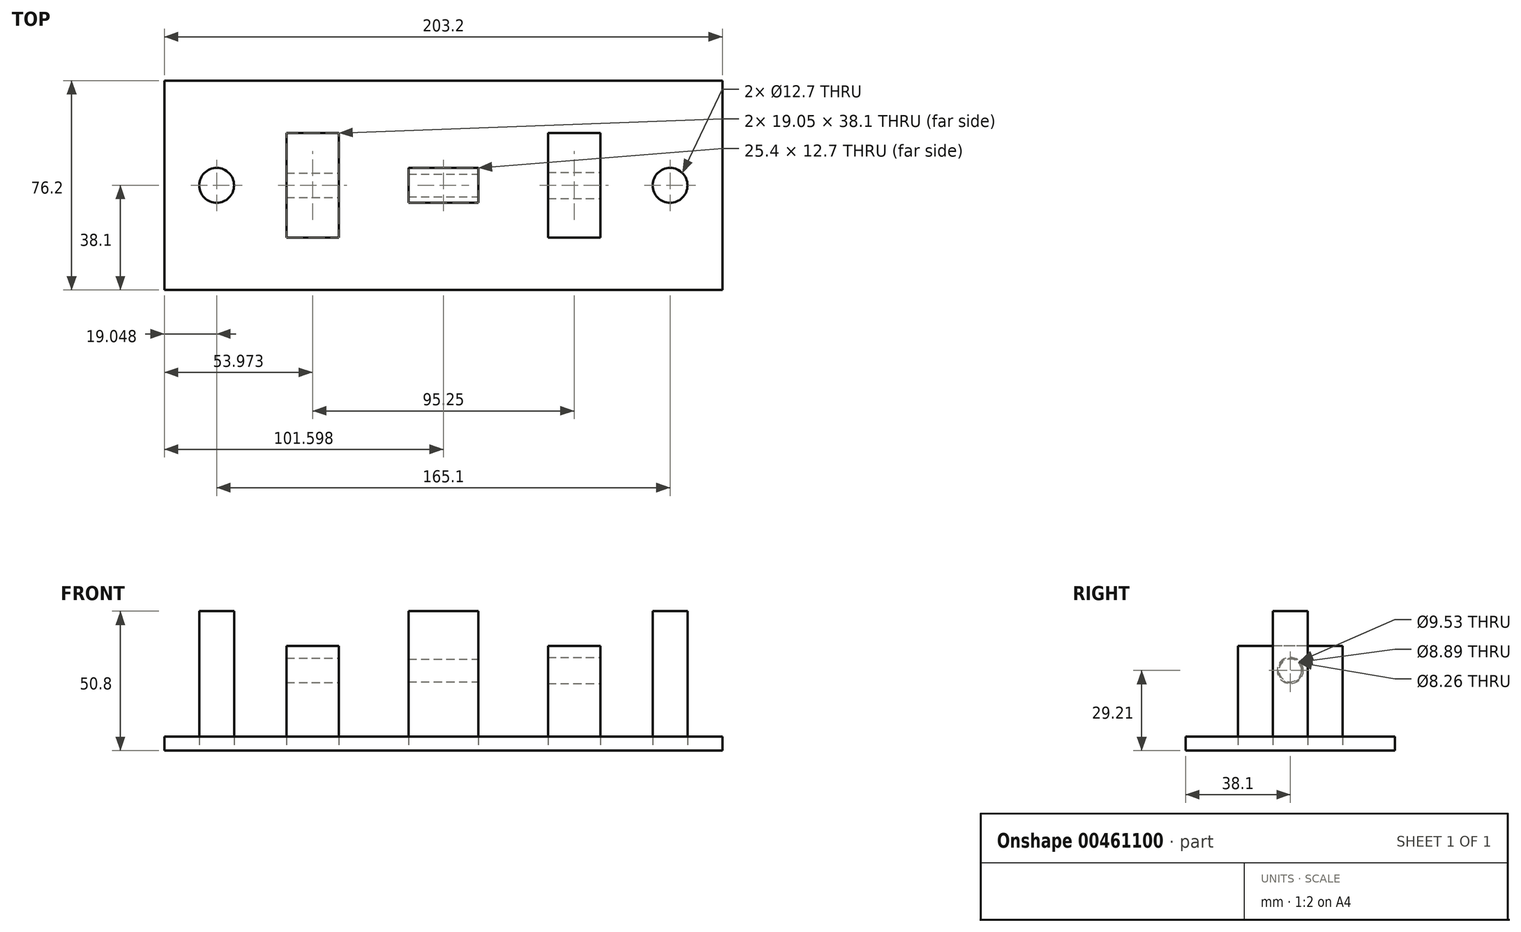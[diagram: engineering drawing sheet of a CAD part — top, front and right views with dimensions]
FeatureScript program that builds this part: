
annotation { "Feature Type Name" : "Feature", "Feature Type Description" : "" }
export const myFeature = defineFeature(function(context is Context, id is Id, definition is map)
    precondition{}
    {
        {
            var Q0;
            Q0=qCreatedBy(makeId("Top.planeOp"),FACE);
            var sketch = newSketch(context, id + "F0", { "sketchPlane" : qUnion([Q0])});
            skLineSegment(sketch, "E0.bottom", {"start": v(-155.23, 38.1) * mm, "end": v(47.97, 38.1) * mm});
            skLineSegment(sketch, "E0.top", {"start": v(-155.23, -38.1) * mm, "end": v(47.97, -38.1) * mm});
            skLineSegment(sketch, "E0.left", {"start": v(-155.23, 38.1) * mm, "end": v(-155.23, -38.1) * mm});
            skLineSegment(sketch, "E0.right", {"start": v(47.97, 38.1) * mm, "end": v(47.97, -38.1) * mm});
            skCircle(sketch, "E1", {"center": v(-136.18, 0) * mm, "radius": 6.35 * mm});
            skCircle(sketch, "E2", {"center": v(28.92, 0) * mm, "radius": 6.35 * mm});
            skLineSegment(sketch, "E3.bottom", {"start": v(-66.33, 6.35) * mm, "end": v(-40.93, 6.35) * mm});
            skLineSegment(sketch, "E3.top", {"start": v(-66.33, -6.35) * mm, "end": v(-40.93, -6.35) * mm});
            skLineSegment(sketch, "E3.left", {"start": v(-66.33, 6.35) * mm, "end": v(-66.33, -6.35) * mm});
            skLineSegment(sketch, "E3.right", {"start": v(-40.93, 6.35) * mm, "end": v(-40.93, -6.35) * mm});
            skPoint(sketch, "E3.middle", {"position": v(-53.63, 0) * mm});
            skLineSegment(sketch, "E4", {"start": v(28.92, 0) * mm, "end": v(47.97, 0) * mm});
            skLineSegment(sketch, "E5.bottom", {"start": v(-110.78, 19.05) * mm, "end": v(-91.73, 19.05) * mm});
            skLineSegment(sketch, "E5.top", {"start": v(-110.78, -19.05) * mm, "end": v(-91.73, -19.05) * mm});
            skLineSegment(sketch, "E5.left", {"start": v(-110.78, 19.05) * mm, "end": v(-110.78, -19.05) * mm});
            skLineSegment(sketch, "E5.right", {"start": v(-91.73, 19.05) * mm, "end": v(-91.73, -19.05) * mm});
            skPoint(sketch, "E5.middle", {"position": v(-101.26, 0) * mm});
            skLineSegment(sketch, "E6.bottom", {"start": v(-15.53, 19.05) * mm, "end": v(3.52, 19.05) * mm});
            skLineSegment(sketch, "E6.top", {"start": v(-15.53, -19.05) * mm, "end": v(3.52, -19.05) * mm});
            skLineSegment(sketch, "E6.left", {"start": v(-15.53, 19.05) * mm, "end": v(-15.53, -19.05) * mm});
            skLineSegment(sketch, "E6.right", {"start": v(3.52, 19.05) * mm, "end": v(3.52, -19.05) * mm});
            skPoint(sketch, "E6.middle", {"position": v(-6, 0) * mm});
            skSolve(sketch);
        }
        {
            var Q0;
            Q0=makeQuery(id+"F0.imprint","IMPRINT",FACE,{"disambiguationData":[TD([[makeQuery(id+"F0.imprint","IMPRINT",EDGE,{"derivedFrom":sQuery(id+"F0.wireOp",EDGE,"E3.bottom")}),-1.0]])]});
            var Q1;
            Q1=makeQuery(id+"F0.imprint","IMPRINT",FACE,{"disambiguationData":[TD([[makeQuery(id+"F0.imprint","IMPRINT",EDGE,{"derivedFrom":sQuery(id+"F0.wireOp",EDGE,"E2")}),1.0]])]});
            var Q2;
            Q2=makeQuery(id+"F0.imprint","IMPRINT",FACE,{"disambiguationData":[TD([[makeQuery(id+"F0.imprint","IMPRINT",EDGE,{"derivedFrom":sQuery(id+"F0.wireOp",EDGE,"E1")}),1.0]])]});
            extrude(context, id + "F1", {"entities" : qUnion([Q0, Q1, Q2]), "depth" : 50.8 * mm});
        }
        {
            var Q0;
            Q0=makeQuery(id+"F0.imprint","IMPRINT",FACE,{"disambiguationData":[TD([[makeQuery(id+"F0.imprint","IMPRINT",EDGE,{"derivedFrom":sQuery(id+"F0.wireOp",EDGE,"E5.bottom")}),-1.0]])]});
            var Q1;
            Q1=makeQuery(id+"F0.imprint","IMPRINT",FACE,{"disambiguationData":[TD([[makeQuery(id+"F0.imprint","IMPRINT",EDGE,{"derivedFrom":sQuery(id+"F0.wireOp",EDGE,"E6.bottom")}),-1.0]])]});
            extrude(context, id + "F2", {"entities" : qUnion([Q0, Q1]), "depth" : 38.1 * mm});
        }
        {
            var Q0;
            {var subQ3=sQuery(id+"F0.wireOp",EDGE,"E0.bottom");Q0=makeQuery(id+"F0.imprint","IMPRINT",FACE,{"disambiguationData":[TD([[makeQuery(id+"F0.imprint","IMPRINT",EDGE,{"derivedFrom":subQ3}),-1.0]])]});}
            extrude(context, id + "F3", {"entities" : qUnion([Q0]), "depth" : 5.08 * mm});
        }
        {
            var Q0;
            Q0=makeQuery(id+"F2.opExtrude","SWEPT_FACE",FACE,{"disambiguationData":[OSD([sQuery(id+"F0.wireOp",EDGE,"E6.right")])]});
            var sketch = newSketch(context, id + "F4", { "sketchPlane" : qUnion([Q0])});
            skCircle(sketch, "E7", {"center": v(0, 29.21) * mm, "radius": 4.76 * mm});
            skLineSegment(sketch, "E8", {"start": v(0, 29.21) * mm, "end": v(0, 38.1) * mm});
            skSolve(sketch);
        }
        {
            var Q0;
            Q0 = qSketchRegion(id + "F4", true);
            extrude(context, id + "F5", {"entities" : qUnion([Q0]), "operationType" : NewBodyOperationType.REMOVE, "oppositeDirection" : true, "depth" : 25.4 * mm});
        }
        {
            var Q0;
            Q0=makeQuery(id+"F1.opExtrude","SWEPT_FACE",FACE,{"disambiguationData":[OSD([sQuery(id+"F0.wireOp",EDGE,"E3.right")])]});
            var sketch = newSketch(context, id + "F6", { "sketchPlane" : qUnion([Q0])});
            skCircle(sketch, "E9", {"center": v(0, 29.21) * mm, "radius": 4.13 * mm});
            skSolve(sketch);
        }
        {
            var Q0;
            Q0 = qSketchRegion(id + "F6", true);
            extrude(context, id + "F7", {"entities" : qUnion([Q0]), "operationType" : NewBodyOperationType.REMOVE, "oppositeDirection" : true, "depth" : 25.4 * mm});
        }
        {
            var Q0;
            Q0=makeQuery(id+"F2.opExtrude","SWEPT_FACE",FACE,{"disambiguationData":[OSD([sQuery(id+"F0.wireOp",EDGE,"E5.right")])]});
            var sketch = newSketch(context, id + "F8", { "sketchPlane" : qUnion([Q0])});
            skCircle(sketch, "E10", {"center": v(0, 29.21) * mm, "radius": 4.45 * mm});
            skSolve(sketch);
        }
        {
            var Q0;
            Q0 = qSketchRegion(id + "F8", true);
            extrude(context, id + "F9", {"entities" : qUnion([Q0]), "operationType" : NewBodyOperationType.REMOVE, "oppositeDirection" : true, "depth" : 25.4 * mm});
        }
    });
